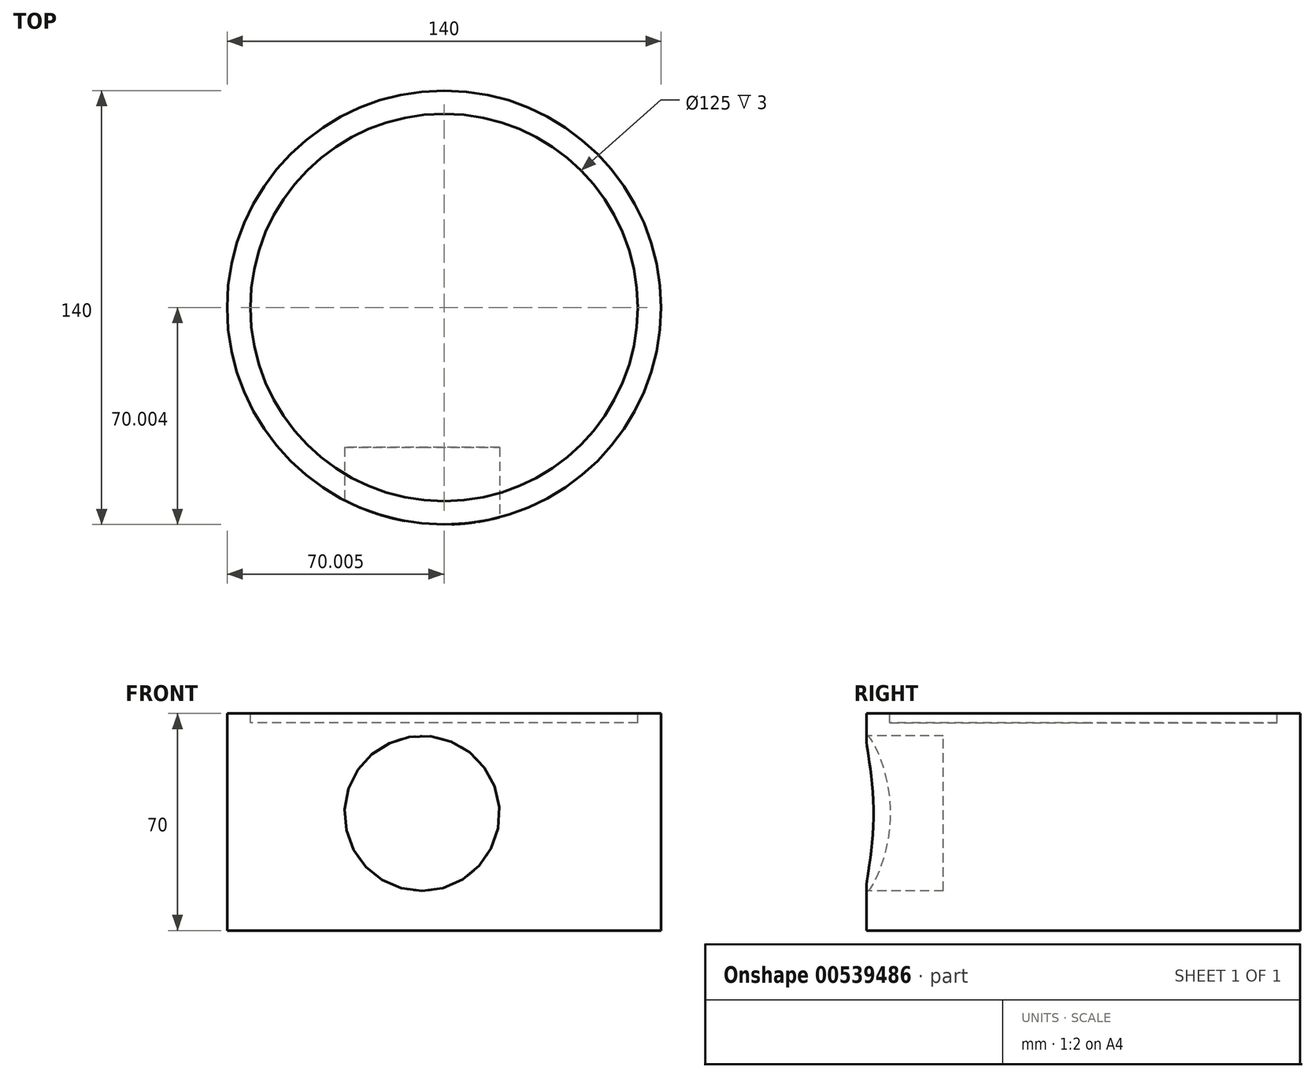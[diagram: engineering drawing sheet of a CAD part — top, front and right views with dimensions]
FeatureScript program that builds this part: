
annotation { "Feature Type Name" : "Feature", "Feature Type Description" : "" }
export const myFeature = defineFeature(function(context is Context, id is Id, definition is map)
    precondition{}
    {
        {
            var Q0;
            Q0=qCreatedBy(makeId("Top.planeOp"),FACE);
            var sketch = newSketch(context, id + "F0", { "sketchPlane" : qUnion([Q0])});
            skCircle(sketch, "E0", {"center": v(-43.57, 8.15) * mm, "radius": 70 * mm});
            skSolve(sketch);
        }
        {
            var Q0;
            Q0=makeQuery(id+"F0.imprint","IMPRINT",FACE,{"disambiguationData":[TD([[makeQuery(id+"F0.imprint","IMPRINT",EDGE,{"derivedFrom":sQuery(id+"F0.wireOp",EDGE,"E0")}),1.0]])]});
            extrude(context, id + "F1", {"entities" : qUnion([Q0]), "depth" : 70 * mm, "offsetDistance" : 25 * mm});
        }
        {
            var Q0;
            Q0=qCreatedBy(makeId("Front.planeOp"),FACE);
            cPlane(context, id + "F2", {"entities" : qUnion([Q0]), "cplaneType" : CPlaneType.OFFSET, "offset" : 62 * mm, "width" : 150 * mm, "height" : 150 * mm});
        }
        {
            var Q0;
            Q0=qCreatedBy(id+"F2.planeOp",FACE);
            var sketch = newSketch(context, id + "F3", { "sketchPlane" : qUnion([Q0])});
            skCircle(sketch, "E1", {"center": v(-50.68, 37.78) * mm, "radius": 25 * mm});
            skSolve(sketch);
        }
        {
            var Q0;
            Q0=makeQuery(id+"F3.imprint","IMPRINT",FACE,{"disambiguationData":[TD([[makeQuery(id+"F3.imprint","IMPRINT",EDGE,{"derivedFrom":sQuery(id+"F3.wireOp",EDGE,"E1")}),1.0]])]});
            extrude(context, id + "F4", {"entities" : qUnion([Q0]), "operationType" : NewBodyOperationType.REMOVE, "oppositeDirection" : true, "depth" : 25 * mm, "offsetDistance" : 25 * mm});
        }
        {
            var Q0;
            Q0=makeQuery(id+"F1.opExtrude","CAP_FACE",FACE,{"disambiguationData":[OSD([sQuery(id+"F0.wireOp",EDGE,"E0")])],"isStart":false});
            var sketch = newSketch(context, id + "F5", { "sketchPlane" : qUnion([Q0])});
            skCircle(sketch, "E2", {"center": v(-43.57, 8.15) * mm, "radius": 62.5 * mm});
            skSolve(sketch);
        }
        {
            var Q0;
            Q0=makeQuery(id+"F5.imprint","IMPRINT",FACE,{"disambiguationData":[TD([[makeQuery(id+"F5.imprint","IMPRINT",EDGE,{"derivedFrom":sQuery(id+"F5.wireOp",EDGE,"E2")}),1.0]])]});
            extrude(context, id + "F6", {"entities" : qUnion([Q0]), "operationType" : NewBodyOperationType.REMOVE, "oppositeDirection" : true, "depth" : 3 * mm, "offsetDistance" : 25 * mm});
        }
    });
